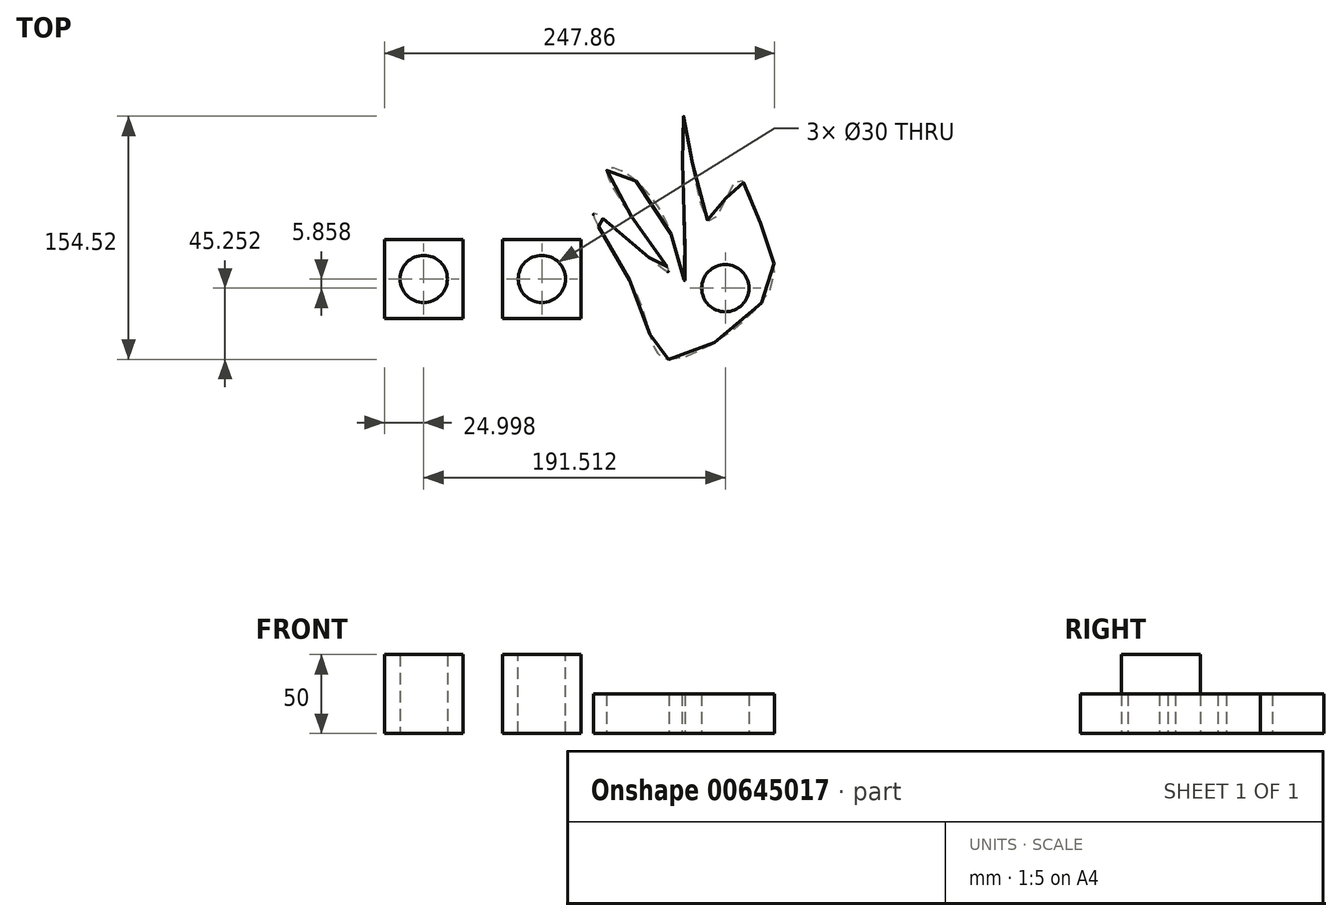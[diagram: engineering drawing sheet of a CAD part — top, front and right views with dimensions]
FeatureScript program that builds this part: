
annotation { "Feature Type Name" : "Feature", "Feature Type Description" : "" }
export const myFeature = defineFeature(function(context is Context, id is Id, definition is map)
    precondition{}
    {
        {
            var Q0;
            Q0=qCreatedBy(makeId("Top.planeOp"),FACE);
            var sketch = newSketch(context, id + "F0", { "sketchPlane" : qUnion([Q0])});
            skLineSegment(sketch, "E0.bottom", {"start": v(-25, -25) * mm, "end": v(25, -25) * mm});
            skLineSegment(sketch, "E0.top", {"start": v(-25, 25) * mm, "end": v(25, 25) * mm});
            skLineSegment(sketch, "E0.left", {"start": v(-25, -25) * mm, "end": v(-25, 25) * mm});
            skLineSegment(sketch, "E0.right", {"start": v(25, -25) * mm, "end": v(25, 25) * mm});
            skPoint(sketch, "E0.middle", {"position": v(0, 0) * mm});
            skSolve(sketch);
        }
        {
            var Q0;
            Q0 = qSketchRegion(id + "F0", true);
            extrude(context, id + "F1", {"entities" : qUnion([Q0]), "depth" : 50 * mm, "offsetDistance" : 25 * mm});
        }
        {
            var Q0;
            Q0=makeQuery(id+"F1.opExtrude","CAP_FACE",FACE,{"disambiguationData":[OSD([sQuery(id+"F0.wireOp",EDGE,"E0.bottom"),sQuery(id+"F0.wireOp",EDGE,"E0.top"),sQuery(id+"F0.wireOp",EDGE,"E0.left"),sQuery(id+"F0.wireOp",EDGE,"E0.right")])],"isStart":false});
            var sketch = newSketch(context, id + "F2", { "sketchPlane" : qUnion([Q0])});
            skCircle(sketch, "E1", {"center": v(0, 0) * mm, "radius": 15 * mm});
            skSolve(sketch);
        }
        {
            var Q0;
            Q0 = qSketchRegion(id + "F2", true);
            extrude(context, id + "F3", {"entities" : qUnion([Q0]), "operationType" : NewBodyOperationType.REMOVE, "oppositeDirection" : true, "depth" : 50 * mm, "offsetDistance" : 25 * mm});
        }
        {
            var Q0;
            Q0=qCreatedBy(makeId("Top.planeOp"),FACE);
            var sketch = newSketch(context, id + "F4", { "sketchPlane" : qUnion([Q0])});
            skLineSegment(sketch, "E2.bottom", {"start": v(-49.98, -25) * mm, "end": v(-99.98, -25) * mm});
            skLineSegment(sketch, "E2.top", {"start": v(-49.98, 25) * mm, "end": v(-99.98, 25) * mm});
            skLineSegment(sketch, "E2.left", {"start": v(-49.98, -25) * mm, "end": v(-49.98, 25) * mm});
            skLineSegment(sketch, "E2.right", {"start": v(-99.98, -25) * mm, "end": v(-99.98, 25) * mm});
            skPoint(sketch, "E2.middle", {"position": v(-74.98, 0) * mm});
            skCircle(sketch, "E3", {"center": v(-74.98, 0) * mm, "radius": 15 * mm});
            skSolve(sketch);
        }
        {
            var Q0;
            Q0 = qSketchRegion(id + "F4", true);
            extrude(context, id + "F5", {"entities" : qUnion([Q0]), "depth" : 25 * mm, "offsetDistance" : 25 * mm});
        }
        {
            var Q0;
            Q0 = qSketchRegion(id + "F4", true);
            extrude(context, id + "F6", {"entities" : qUnion([Q0]), "operationType" : NewBodyOperationType.REMOVE, "oppositeDirection" : true, "depth" : 50 * mm, "offsetDistance" : 25 * mm});
        }
        {
            var Q0;
            Q0 = qSketchRegion(id + "F4", true);
            extrude(context, id + "F7", {"entities" : qUnion([Q0]), "operationType" : NewBodyOperationType.ADD, "depth" : 50 * mm, "offsetDistance" : 25 * mm});
        }
        {
            var Q0;
            Q0=qCreatedBy(makeId("Top.planeOp"),FACE);
            var sketch = newSketch(context, id + "F8", { "sketchPlane" : qUnion([Q0])});
            skFitSpline(sketch, "E4", {"points": [v(80.37, -51.02) * mm, v(144.2, -8.33) * mm, v(139.2, 34.35) * mm, v(123.55, 62.72) * mm, v(106.56, 36.34) * mm, v(89.94, 103.4) * mm, v(90.93, 0) * mm, v(73.47, 46.58) * mm, v(41.24, 67.8) * mm, v(80.5, 4.57) * mm, v(33.91, 41.5) * mm, v(61.23, -12.44) * mm, v(80.37, -51.02) * mm]});
            skCircle(sketch, "E5", {"center": v(116.53, -5.86) * mm, "radius": 15 * mm});
            skSolve(sketch);
        }
        {
            var Q0;
            Q0=makeQuery(id+"F8.imprint","IMPRINT",FACE,{"disambiguationData":[TD([[makeQuery(id+"F8.imprint","IMPRINT",EDGE,{"derivedFrom":sQuery(id+"F8.wireOp",EDGE,"E4")}),1.0]])]});
            extrude(context, id + "F9", {"entities" : qUnion([Q0]), "depth" : 25 * mm, "offsetDistance" : 25 * mm});
        }
    });
